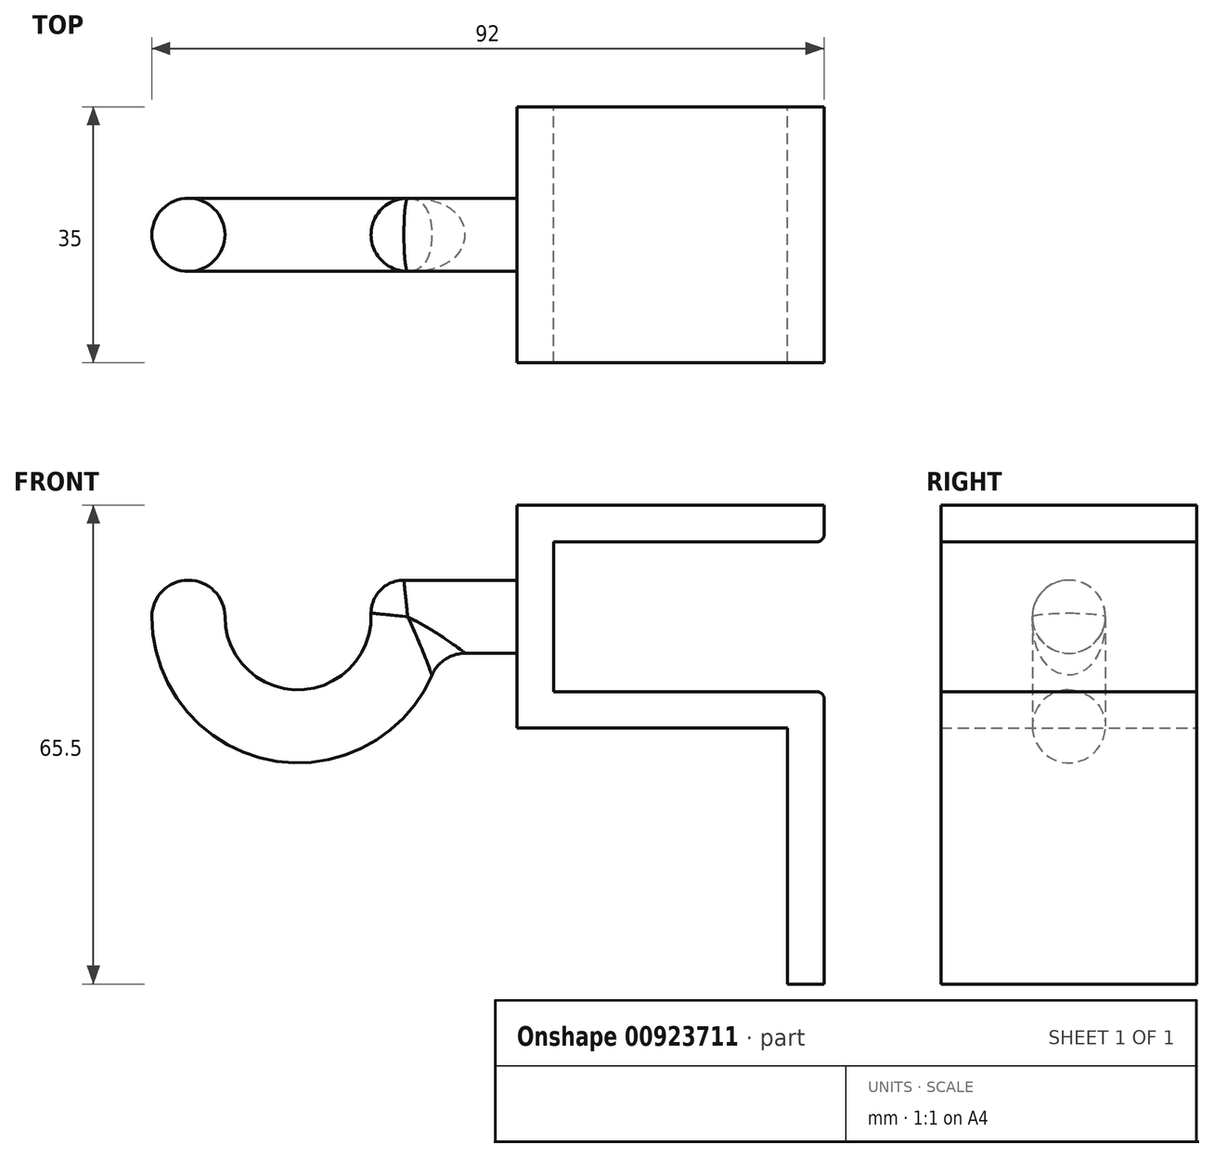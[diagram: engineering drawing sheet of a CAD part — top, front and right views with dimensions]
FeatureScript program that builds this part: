
annotation { "Feature Type Name" : "Feature", "Feature Type Description" : "" }
export const myFeature = defineFeature(function(context is Context, id is Id, definition is map)
    precondition{}
    {
        {
            var Q0;
            Q0=qCreatedBy(makeId("Front.planeOp"),FACE);
            var sketch = newSketch(context, id + "F0", { "sketchPlane" : qUnion([Q0])});
            skLineSegment(sketch, "E0", {"start": v(0, 0) * mm, "end": v(0, -30.5) * mm});
            skLineSegment(sketch, "E1", {"start": v(42, -65.5) * mm, "end": v(42, -25.5) * mm});
            skLineSegment(sketch, "E2", {"start": v(42, -25.5) * mm, "end": v(5, -25.5) * mm});
            skLineSegment(sketch, "E3", {"start": v(5, -25.5) * mm, "end": v(5, -5) * mm});
            skLineSegment(sketch, "E4", {"start": v(5, -5) * mm, "end": v(42, -5) * mm});
            skLineSegment(sketch, "E5", {"start": v(42, -5) * mm, "end": v(42, 0) * mm});
            skLineSegment(sketch, "E6", {"start": v(42, 0) * mm, "end": v(0, 0) * mm});
            skLineSegment(sketch, "E7", {"start": v(0, -30.5) * mm, "end": v(37, -30.5) * mm});
            skLineSegment(sketch, "E8", {"start": v(37, -30.5) * mm, "end": v(37, -65.5) * mm});
            skLineSegment(sketch, "E9", {"start": v(37, -65.5) * mm, "end": v(42, -65.5) * mm});
            skSolve(sketch);
        }
        {
            var Q0;
            Q0 = qSketchRegion(id + "F0", true);
            extrude(context, id + "F1", {"entities" : qUnion([Q0]), "endBound" : BoundingType.SYMMETRIC, "depth" : 35 * mm, "offsetDistance" : 25 * mm});
        }
        {
            var Q0;
            Q0=makeQuery(id+"F1.opExtrude","SWEPT_FACE",FACE,{"disambiguationData":[OSD([sQuery(id+"F0.wireOp",EDGE,"E0")])]});
            var sketch = newSketch(context, id + "F2", { "sketchPlane" : qUnion([Q0])});
            skCircle(sketch, "E10", {"center": v(0, -15.25) * mm, "radius": 5 * mm});
            skLineSegment(sketch, "E11", {"start": v(0, 0) * mm, "end": v(0, -15.25) * mm, "construction": true});
            skLineSegment(sketch, "E12", {"start": v(0, -30.5) * mm, "end": v(0, -15.25) * mm, "construction": true});
            skSolve(sketch);
        }
        {
            var Q0;
            Q0=qCreatedBy(makeId("Front.planeOp"),FACE);
            var sketch = newSketch(context, id + "F3", { "sketchPlane" : qUnion([Q0])});
            skPoint(sketch, "E13.0", {"position": v(0, -15.25) * mm});
            skLineSegment(sketch, "E14", {"start": v(0, -15.25) * mm, "end": v(-15, -15.25) * mm});
            skArc(sketch, "E15", {"start": v(-45, -15.25) * mm, "mid": v(-30, -30.25) * mm, "end": v(-15, -15.25) * mm});
            skLineSegment(sketch, "E16", {"start": v(-45, -15.25) * mm, "end": v(-15, -15.25) * mm, "construction": true});
            skSolve(sketch);
        }
        {
            var Q0;
            Q0 = qSketchRegion(id + "F2", true);
            var Q1;
            Q1 = qConstructionFilter(qBodyType(qCreatedBy(id + "F3" ,EDGE), BodyType.WIRE), ConstructionObject.NO);
            sweep(context, id + "F4", {"operationType" : NewBodyOperationType.ADD, "profiles" : qUnion([Q0]), "path" : qUnion([Q1])});
        }
        {
            var Q0;
            Q0=makeQuery(id+"F4.opSweep","CAP_FACE",FACE,{"disambiguationData":[OSD([sQuery(id+"F2.wireOp",EDGE,"E10"),sQuery(id+"F3.wireOp",VERTEX,"E15.start")])],"isStart":false});
            var sketch = newSketch(context, id + "F5", { "sketchPlane" : qUnion([Q0])});
            skLineSegment(sketch, "E17", {"start": v(-50, 0) * mm, "end": v(-40, 0) * mm});
            skArc(sketch, "E18.0", {"start": v(-40, 0) * mm, "mid": v(-45, 5) * mm, "end": v(-50, 0) * mm});
            skSolve(sketch);
        }
        {
            var Q0;
            Q0 = qSketchRegion(id + "F5", true);
            var Q1;
            Q1=sQuery(id+"F5.wireOp",EDGE,"E17");
            revolve(context, id + "F6", {"operationType" : NewBodyOperationType.ADD, "surfaceOperationType" : NewSurfaceOperationType.NEW, "entities" : qUnion([Q0]), "axis" : qUnion([Q1]), "revolveType" : RevolveType.FULL});
        }
        {
            var Q0;
            Q0=makeQuery(id+"F4.opSweep","MID_CAP_EDGE",EDGE,{"disambiguationData":[OSD([sQuery(id+"F2.wireOp",EDGE,"E10"),sQuery(id+"F3.wireOp",VERTEX,"E15.end")]),OD(0.0)],"capPos":1.0});
            var Q1;
            Q1=makeQuery(id+"F4.opSweep","CAP_EDGE",EDGE,{"disambiguationData":[OSD([sQuery(id+"F2.wireOp",EDGE,"E10"),sQuery(id+"F3.wireOp",VERTEX,"E14.start")])],"isStart":true});
            fillet(context, id + "F7", {"entities" : qUnion([Q0, Q1]), "radius" : 5 * mm, "tangentPropagation" : true, "allowEdgeOverflow" : false});
        }
        {
            var Q0;
            Q0=makeQuery(id+"F1.opExtrude","SWEPT_EDGE",EDGE,{"disambiguationData":[OSD([sQuery(id+"F0.wireOp",EDGE,"E4"),sQuery(id+"F0.wireOp",EDGE,"E5")])]});
            var Q1;
            Q1=makeQuery(id+"F1.opExtrude","SWEPT_EDGE",EDGE,{"disambiguationData":[OSD([sQuery(id+"F0.wireOp",EDGE,"E1"),sQuery(id+"F0.wireOp",EDGE,"E2")])]});
            fillet(context, id + "F8", {"entities" : qUnion([Q0, Q1]), "radius" : 1 * mm, "tangentPropagation" : true, "allowEdgeOverflow" : false});
        }
        {
            var Q0;
            Q0=makeQuery(id+"F4.opSweep","MID_CAP_EDGE",EDGE,{"disambiguationData":[OSD([sQuery(id+"F2.wireOp",EDGE,"E10"),sQuery(id+"F3.wireOp",VERTEX,"E15.end")]),OD(1.0)],"capPos":1.0});
            fillet(context, id + "F9", {"entities" : qUnion([Q0]), "radius" : 4.5 * mm, "tangentPropagation" : true, "allowEdgeOverflow" : false});
        }
    });
